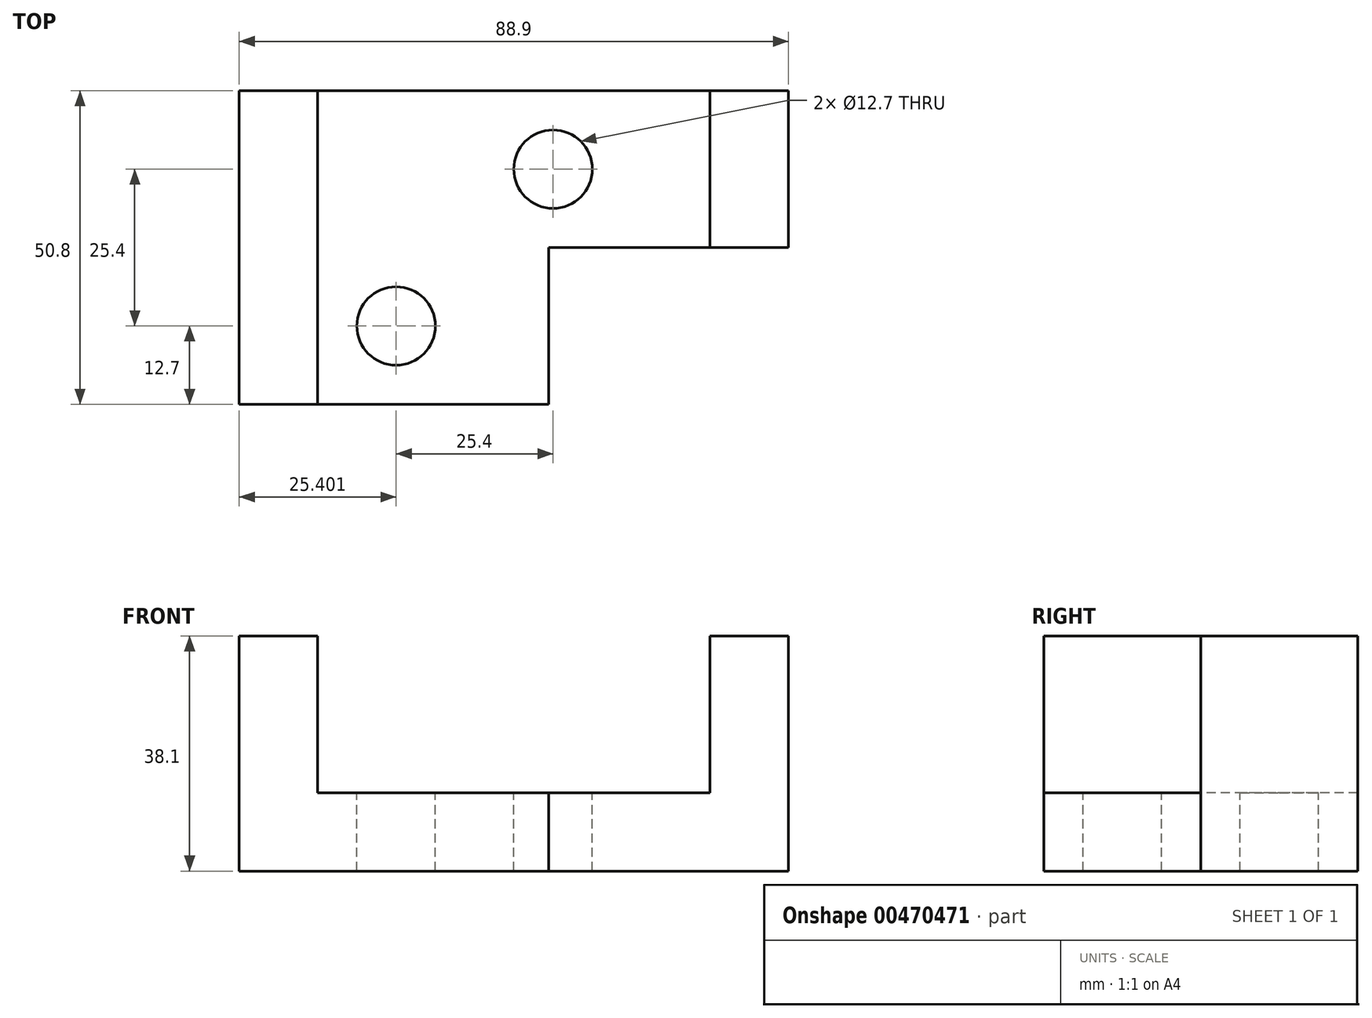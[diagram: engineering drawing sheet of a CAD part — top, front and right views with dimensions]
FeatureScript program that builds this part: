
annotation { "Feature Type Name" : "Feature", "Feature Type Description" : "" }
export const myFeature = defineFeature(function(context is Context, id is Id, definition is map)
    precondition{}
    {
        {
            var Q0;
            Q0=qCreatedBy(makeId("Front.planeOp"),FACE);
            var sketch = newSketch(context, id + "F0", { "sketchPlane" : qUnion([Q0])});
            skLineSegment(sketch, "E0.bottom", {"start": v(-50.1, 15.81) * mm, "end": v(38.8, 15.81) * mm});
            skLineSegment(sketch, "E0.top", {"start": v(-50.1, -22.29) * mm, "end": v(38.8, -22.29) * mm});
            skLineSegment(sketch, "E0.left", {"start": v(-50.1, 15.81) * mm, "end": v(-50.1, -22.29) * mm});
            skLineSegment(sketch, "E0.right", {"start": v(38.8, 15.81) * mm, "end": v(38.8, -22.29) * mm});
            skSolve(sketch);
        }
        {
            var Q0;
            Q0=makeQuery(id+"F0.imprint","IMPRINT",FACE,{"disambiguationData":[TD([[makeQuery(id+"F0.imprint","IMPRINT",EDGE,{"derivedFrom":sQuery(id+"F0.wireOp",EDGE,"E0.bottom")}),-1.0]])]});
            extrude(context, id + "F1", {"entities" : qUnion([Q0]), "depth" : 50.8 * mm});
        }
        {
            var Q0;
            Q0=makeQuery(id+"F1.opExtrude","CAP_FACE",FACE,{"disambiguationData":[OSD([sQuery(id+"F0.wireOp",EDGE,"E0.bottom"),sQuery(id+"F0.wireOp",EDGE,"E0.top"),sQuery(id+"F0.wireOp",EDGE,"E0.left"),sQuery(id+"F0.wireOp",EDGE,"E0.right")])],"isStart":false});
            var sketch = newSketch(context, id + "F2", { "sketchPlane" : qUnion([Q0])});
            skLineSegment(sketch, "E1.bottom", {"start": v(-37.4, 15.81) * mm, "end": v(26.1, 15.81) * mm});
            skLineSegment(sketch, "E1.top", {"start": v(-37.4, -9.59) * mm, "end": v(26.1, -9.59) * mm});
            skLineSegment(sketch, "E1.left", {"start": v(-37.4, 15.81) * mm, "end": v(-37.4, -9.59) * mm});
            skLineSegment(sketch, "E1.right", {"start": v(26.1, 15.81) * mm, "end": v(26.1, -9.59) * mm});
            skSolve(sketch);
        }
        {
            var Q0;
            Q0=makeQuery(id+"F2.imprint","IMPRINT",FACE,{"disambiguationData":[TD([[makeQuery(id+"F2.imprint","IMPRINT",EDGE,{"derivedFrom":sQuery(id+"F2.wireOp",EDGE,"E1.bottom")}),-1.0]])]});
            extrude(context, id + "F3", {"entities" : qUnion([Q0]), "operationType" : NewBodyOperationType.REMOVE, "endBound" : BoundingType.THROUGH_ALL, "oppositeDirection" : true, "depth" : 25.4 * mm});
        }
        {
            var Q0;
            Q0=makeQuery(id+"F1.opExtrude","CAP_FACE",FACE,{"disambiguationData":[OSD([sQuery(id+"F0.wireOp",EDGE,"E0.bottom"),sQuery(id+"F0.wireOp",EDGE,"E0.top"),sQuery(id+"F0.wireOp",EDGE,"E0.left"),sQuery(id+"F0.wireOp",EDGE,"E0.right")])],"isStart":false});
            var sketch = newSketch(context, id + "F4", { "sketchPlane" : qUnion([Q0])});
            skLineSegment(sketch, "E2", {"start": v(0, -9.59) * mm, "end": v(0, -22.29) * mm});
            skLineSegment(sketch, "E3", {"start": v(0, -22.29) * mm, "end": v(38.8, -22.29) * mm});
            skSolve(sketch);
        }
        {
            var Q0;
            {var subQ3=sQuery(id+"F4.wireOp",EDGE,"E2");Q0=makeQuery(id+"F4.imprint","IMPRINT",FACE,{"disambiguationData":[TD([[makeQuery(id+"F4.imprint","IMPRINT",EDGE,{"derivedFrom":subQ3}),1.0]])]});}
            extrude(context, id + "F5", {"entities" : qUnion([Q0]), "operationType" : NewBodyOperationType.REMOVE, "oppositeDirection" : true, "depth" : 25.4 * mm});
        }
        {
            var Q0;
            Q0=makeQuery(id+"F3.boolean.opBoolean","COPY",FACE,{"derivedFrom":makeQuery(id+"F3.opExtrude","SWEPT_FACE",FACE,{"disambiguationData":[OSD([sQuery(id+"F2.wireOp",EDGE,"E1.top")])]})});
            var sketch = newSketch(context, id + "F6", { "sketchPlane" : qUnion([Q0])});
            skCircle(sketch, "E4", {"center": v(0.7, -12.7) * mm, "radius": 6.35 * mm});
            skSolve(sketch);
        }
        {
            var Q0;
            Q0=makeQuery(id+"F6.imprint","IMPRINT",FACE,{"disambiguationData":[TD([[makeQuery(id+"F6.imprint","IMPRINT",EDGE,{"derivedFrom":sQuery(id+"F6.wireOp",EDGE,"E4")}),-1.0]])]});
            var sketch = newSketch(context, id + "F7", { "sketchPlane" : qUnion([Q0])});
            skCircle(sketch, "E5", {"center": v(-24.7, -38.1) * mm, "radius": 6.35 * mm});
            skSolve(sketch);
        }
        {
            var Q0;
            Q0=makeQuery(id+"F6.imprint","IMPRINT",FACE,{"disambiguationData":[TD([[makeQuery(id+"F6.imprint","IMPRINT",EDGE,{"derivedFrom":sQuery(id+"F6.wireOp",EDGE,"E4")}),1.0]])]});
            extrude(context, id + "F8", {"entities" : qUnion([Q0]), "operationType" : NewBodyOperationType.REMOVE, "endBound" : BoundingType.THROUGH_ALL, "oppositeDirection" : true, "depth" : 25.4 * mm});
        }
        {
            var Q0;
            Q0=makeQuery(id+"F7.imprint","IMPRINT",FACE,{"disambiguationData":[TD([[makeQuery(id+"F7.imprint","IMPRINT",EDGE,{"derivedFrom":sQuery(id+"F7.wireOp",EDGE,"E5")}),1.0]])]});
            extrude(context, id + "F9", {"entities" : qUnion([Q0]), "operationType" : NewBodyOperationType.ADD, "endBound" : BoundingType.THROUGH_ALL, "depth" : 25.4 * mm});
        }
        {
            var Q0;
            Q0=makeQuery(id+"F9.opExtrude","CAP_FACE",FACE,{"disambiguationData":[OSD([sQuery(id+"F7.wireOp",EDGE,"E5")])],"isStart":false});
            extrude(context, id + "F10", {"entities" : qUnion([Q0]), "operationType" : NewBodyOperationType.REMOVE, "endBound" : BoundingType.THROUGH_ALL, "oppositeDirection" : true, "depth" : 25.4 * mm});
        }
    });
